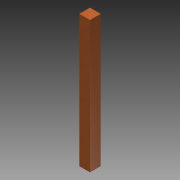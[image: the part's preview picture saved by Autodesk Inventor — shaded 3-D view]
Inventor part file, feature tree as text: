
AUTODESK INVENTOR PART (.ipt)
format: ipt  version: 2015 (Build 190159000, 159)  size: 72,704 bytes
history: native  units: in
note: dims shown in document units (in); Inventor stores cm internally (conversion verified against a paired STEP export)
features: extrude x1, sketch x1
ambient origin geometry x8: Origin, YZ Plane, XZ Plane, XY Plane, X Axis, Y Axis, Z Axis, Center Point
bodies: Solid1 (feature_tree)
feature tree (2):
  extrude  "Extrusion1"  Depth=43.25in TaperAngle=0.0deg
  sketch  "Sketch1"  dims[d0=3.5in d1=43.25in d2=0.0in]
